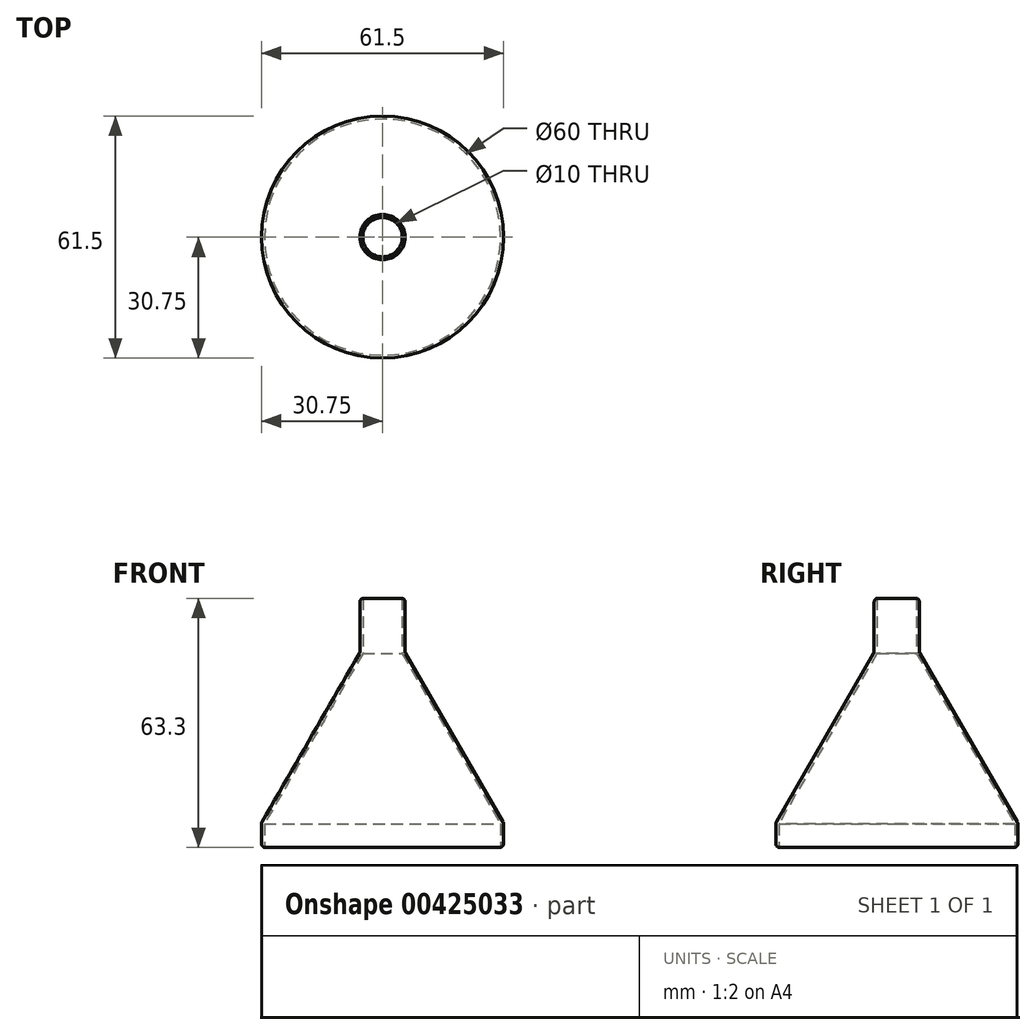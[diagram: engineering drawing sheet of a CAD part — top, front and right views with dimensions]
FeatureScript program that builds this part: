
annotation { "Feature Type Name" : "Feature", "Feature Type Description" : "" }
export const myFeature = defineFeature(function(context is Context, id is Id, definition is map)
    precondition{}
    {
        {
            var Q0;
            Q0=qCreatedBy(makeId("Front.planeOp"),FACE);
            var sketch = newSketch(context, id + "F0", { "sketchPlane" : qUnion([Q0])});
            skLineSegment(sketch, "E0", {"start": v(0, -39.72) * mm, "end": v(0, 56.13) * mm, "construction": true});
            skLineSegment(sketch, "E1", {"start": v(-30, 0) * mm, "end": v(-30, 6) * mm});
            skLineSegment(sketch, "E2", {"start": v(-30, 6) * mm, "end": v(-5, 49.3) * mm});
            skLineSegment(sketch, "E3", {"start": v(-5, 49.3) * mm, "end": v(-5, 63.3) * mm});
            skLineSegment(sketch, "E4.0", {"start": v(-5.75, 49.5) * mm, "end": v(-5.75, 63.3) * mm});
            skLineSegment(sketch, "E4.1", {"start": v(-30.75, 6.2) * mm, "end": v(-5.75, 49.5) * mm});
            skLineSegment(sketch, "E4.2", {"start": v(-30.75, 0) * mm, "end": v(-30.75, 6.2) * mm});
            skLineSegment(sketch, "E5", {"start": v(-5.75, 63.3) * mm, "end": v(-5, 63.3) * mm});
            skLineSegment(sketch, "E6", {"start": v(-30.75, 0) * mm, "end": v(-30, 0) * mm});
            skSolve(sketch);
        }
        {
            var Q0;
            Q0=makeQuery(id+"F0.imprint","IMPRINT",FACE,{"disambiguationData":[TD([[makeQuery(id+"F0.imprint","IMPRINT",EDGE,{"derivedFrom":sQuery(id+"F0.wireOp",EDGE,"E1")}),1.0]])]});
            var Q1;
            Q1=sQuery(id+"F0.wireOp",EDGE,"E0");
            revolve(context, id + "F1", {"entities" : qUnion([Q0]), "axis" : qUnion([Q1]), "revolveType" : RevolveType.FULL});
        }
        {
            var Q0;
            Q0=makeQuery(id+"F1.opRevolve","SWEPT_EDGE",EDGE,{"disambiguationData":[OSD([sQuery(id+"F0.wireOp",EDGE,"E4.0"),sQuery(id+"F0.wireOp",EDGE,"E5")])]});
            var Q1;
            Q1=makeQuery(id+"F1.opRevolve","SWEPT_EDGE",EDGE,{"disambiguationData":[OSD([sQuery(id+"F0.wireOp",EDGE,"E4.0"),sQuery(id+"F0.wireOp",EDGE,"E4.1")])]});
            var Q2;
            Q2=makeQuery(id+"F1.opRevolve","SWEPT_EDGE",EDGE,{"disambiguationData":[OSD([sQuery(id+"F0.wireOp",EDGE,"E4.1"),sQuery(id+"F0.wireOp",EDGE,"E4.2")])]});
            var Q3;
            Q3=makeQuery(id+"F1.opRevolve","SWEPT_EDGE",EDGE,{"disambiguationData":[OSD([sQuery(id+"F0.wireOp",EDGE,"E4.2"),sQuery(id+"F0.wireOp",EDGE,"E6")])]});
            fillet(context, id + "F2", {"entities" : qUnion([Q0, Q1, Q2, Q3]), "radius" : 1 * mm, "tangentPropagation" : true, "allowEdgeOverflow" : false});
        }
    });
